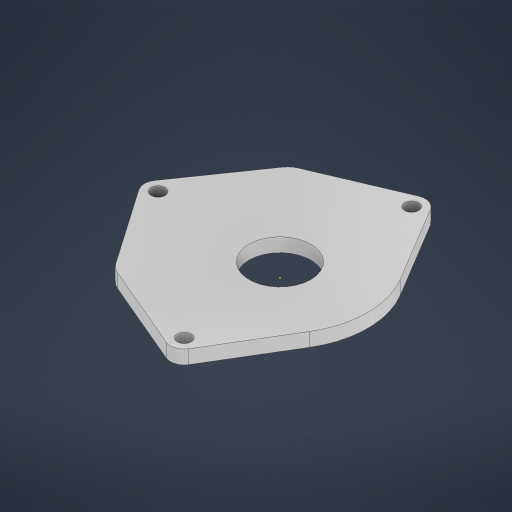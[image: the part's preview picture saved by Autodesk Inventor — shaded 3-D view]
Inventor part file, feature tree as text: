
AUTODESK INVENTOR PART (.ipt)
format: ipt  version: 2024.3 (Build 283343000, 343)  size: 240,128 bytes
history: native  units: in
note: dims shown in document units (in); Inventor stores cm internally (conversion verified against a paired STEP export)
features: sketch x2, extrude x1
ambient origin geometry x8: Origin, YZ Plane, XZ Plane, XY Plane, X Axis, Y Axis, Z Axis, Center Point
bodies: Body1 (feature_tree)
feature tree (3):
  sketch  "Sketch1"  dims[d0=0.5in d1=3.0in]
  sketch  "Sketch2"  dims[d2=0.5in d3=2.36in d4=2.36in d5=0.25in d6=0.1in d8=0.5in d9=0.257in d11=0.25in d12=0.5in d13=0.257in d14=0.25in d15=0.5in d16=0.257in d17=0.25in d18=0.25in d19=1.125in d20=0.75in d21=2.0in d22=0.22in d23=2.7559in d25=360.0deg d27=2.0in d28=2.7559in d30=360.0deg d34=0.25in d35=0.0in]
  extrude  "Extrusion2"  Depth=3.0in
